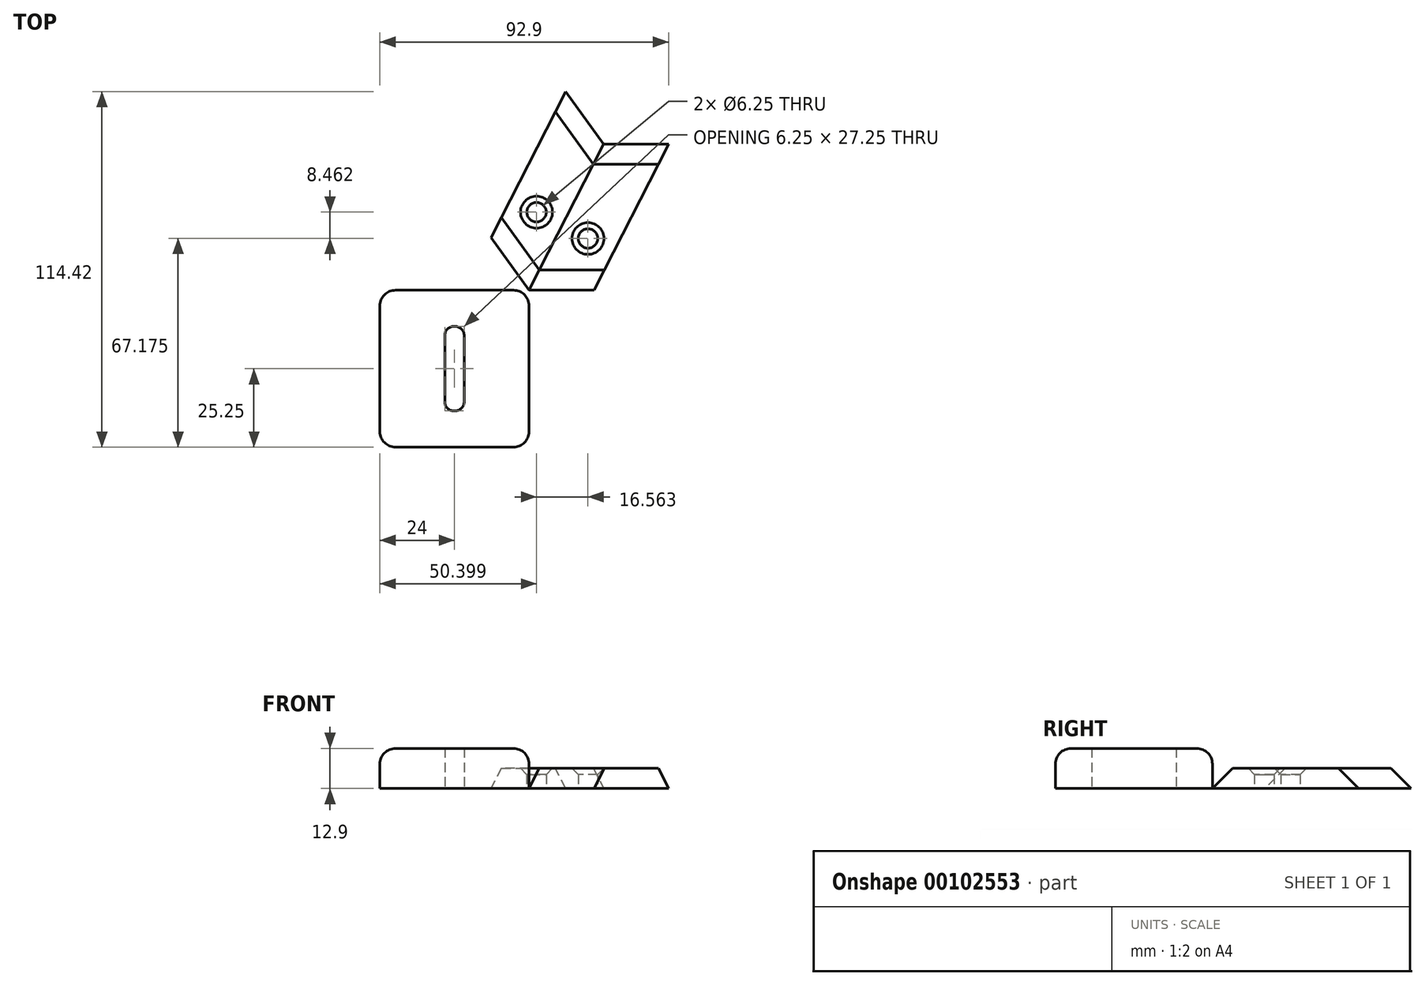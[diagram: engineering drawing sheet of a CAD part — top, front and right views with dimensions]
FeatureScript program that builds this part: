
annotation { "Feature Type Name" : "Feature", "Feature Type Description" : "" }
export const myFeature = defineFeature(function(context is Context, id is Id, definition is map)
    precondition{}
    {
        {
            var Q0;
            Q0=qCreatedBy(makeId("Top.planeOp"),FACE);
            var sketch = newSketch(context, id + "F0", { "sketchPlane" : qUnion([Q0])});
            skLineSegment(sketch, "E0.bottom", {"start": v(-43, -50.5) * mm, "end": v(-5, -50.5) * mm});
            skLineSegment(sketch, "E0.top", {"start": v(-43, 0) * mm, "end": v(-5, 0) * mm});
            skLineSegment(sketch, "E0.left", {"start": v(-48, -45.5) * mm, "end": v(-48, -5) * mm});
            skLineSegment(sketch, "E0.right", {"start": v(0, -45.5) * mm, "end": v(0, -5) * mm});
            skLineSegment(sketch, "E1.bottom", {"start": v(-24.13, -11.62) * mm, "end": v(-23.87, -11.62) * mm});
            skLineSegment(sketch, "E1.top", {"start": v(-24.13, -38.88) * mm, "end": v(-23.87, -38.88) * mm});
            skLineSegment(sketch, "E1.left", {"start": v(-27.13, -14.62) * mm, "end": v(-27.13, -35.88) * mm});
            skLineSegment(sketch, "E1.right", {"start": v(-20.87, -14.62) * mm, "end": v(-20.87, -35.88) * mm});
            skPoint(sketch, "E2", {"position": v(-24, -11.62) * mm});
            skPoint(sketch, "E3", {"position": v(-20.87, -25.25) * mm});
            skPoint(sketch, "E4", {"position": v(-27.13, -25.25) * mm});
            skPoint(sketch, "E5", {"position": v(-24, -38.88) * mm});
            skPoint(sketch, "E6", {"position": v(-24, 0) * mm});
            skPoint(sketch, "E7", {"position": v(-24, -50.5) * mm});
            skPoint(sketch, "E8", {"position": v(0, -25.25) * mm});
            skPoint(sketch, "E9", {"position": v(-48, -25.25) * mm});
            skPoint(sketch, "E10.visualSharp", {"position": v(-27.13, -11.62) * mm});
            skArc(sketch, "E10.filletArc", {"start": v(-24.13, -11.62) * mm, "mid": v(-26.25, -12.5) * mm, "end": v(-27.13, -14.62) * mm});
            skPoint(sketch, "E11.visualSharp", {"position": v(-20.87, -11.62) * mm});
            skArc(sketch, "E11.filletArc", {"start": v(-20.87, -14.62) * mm, "mid": v(-21.75, -12.5) * mm, "end": v(-23.87, -11.62) * mm});
            skPoint(sketch, "E12.visualSharp", {"position": v(-27.13, -38.88) * mm});
            skArc(sketch, "E12.filletArc", {"start": v(-27.13, -35.88) * mm, "mid": v(-26.25, -38) * mm, "end": v(-24.13, -38.88) * mm});
            skPoint(sketch, "E13.visualSharp", {"position": v(-20.87, -38.88) * mm});
            skArc(sketch, "E13.filletArc", {"start": v(-23.87, -38.88) * mm, "mid": v(-21.75, -38) * mm, "end": v(-20.87, -35.88) * mm});
            skPoint(sketch, "E14.visualSharp", {"position": v(-48, 0) * mm});
            skArc(sketch, "E14.filletArc", {"start": v(-43, 0) * mm, "mid": v(-46.54, -1.46) * mm, "end": v(-48, -5) * mm});
            skPoint(sketch, "E15.visualSharp", {"position": v(-48, -50.5) * mm});
            skArc(sketch, "E15.filletArc", {"start": v(-48, -45.5) * mm, "mid": v(-46.54, -49.04) * mm, "end": v(-43, -50.5) * mm});
            skPoint(sketch, "E16.visualSharp", {"position": v(0, -50.5) * mm});
            skArc(sketch, "E16.filletArc", {"start": v(-5, -50.5) * mm, "mid": v(-1.46, -49.04) * mm, "end": v(0, -45.5) * mm});
            skPoint(sketch, "E17.visualSharp", {"position": v(0, 0) * mm});
            skArc(sketch, "E17.filletArc", {"start": v(0, -5) * mm, "mid": v(-1.46, -1.46) * mm, "end": v(-5, 0) * mm});
            skSolve(sketch);
        }
        {
            var Q0;
            Q0=makeQuery(id+"F0.imprint","IMPRINT",FACE,{"disambiguationData":[TD([[makeQuery(id+"F0.imprint","IMPRINT",EDGE,{"derivedFrom":sQuery(id+"F0.wireOp",EDGE,"E0.bottom")}),1.0]])]});
            extrude(context, id + "F1", {"entities" : qUnion([Q0]), "depth" : 12.9 * mm});
        }
        {
            var Q0;
            Q0=makeQuery(id+"F1.opExtrude","CAP_EDGE",EDGE,{"disambiguationData":[OSD([sQuery(id+"F0.wireOp",EDGE,"E0.right")])],"isStart":false});
            var Q1;
            Q1=makeQuery(id+"F1.opExtrude","CAP_EDGE",EDGE,{"disambiguationData":[OSD([sQuery(id+"F0.wireOp",EDGE,"E16.filletArc")])],"isStart":false});
            var Q2;
            Q2=makeQuery(id+"F1.opExtrude","CAP_EDGE",EDGE,{"disambiguationData":[OSD([sQuery(id+"F0.wireOp",EDGE,"E0.bottom")])],"isStart":false});
            var Q3;
            Q3=makeQuery(id+"F1.opExtrude","CAP_EDGE",EDGE,{"disambiguationData":[OSD([sQuery(id+"F0.wireOp",EDGE,"E15.filletArc")])],"isStart":false});
            var Q4;
            Q4=makeQuery(id+"F1.opExtrude","CAP_EDGE",EDGE,{"disambiguationData":[OSD([sQuery(id+"F0.wireOp",EDGE,"E0.left")])],"isStart":false});
            var Q5;
            Q5=makeQuery(id+"F1.opExtrude","CAP_EDGE",EDGE,{"disambiguationData":[OSD([sQuery(id+"F0.wireOp",EDGE,"E14.filletArc")])],"isStart":false});
            var Q6;
            Q6=makeQuery(id+"F1.opExtrude","CAP_EDGE",EDGE,{"disambiguationData":[OSD([sQuery(id+"F0.wireOp",EDGE,"E0.top")])],"isStart":false});
            var Q7;
            Q7=makeQuery(id+"F1.opExtrude","CAP_EDGE",EDGE,{"disambiguationData":[OSD([sQuery(id+"F0.wireOp",EDGE,"E17.filletArc")])],"isStart":false});
            fillet(context, id + "F2", {"entities" : qUnion([Q0, Q1, Q2, Q3, Q4, Q5, Q6, Q7]), "radius" : 5 * mm, "tangentPropagation" : true, "allowEdgeOverflow" : false});
        }
        {
            var Q0;
            Q0=qCreatedBy(makeId("Top.planeOp"),FACE);
            var sketch = newSketch(context, id + "F3", { "sketchPlane" : qUnion([Q0])});
            skLineSegment(sketch, "E18", {"start": v(0, 0) * mm, "end": v(20.89, 0) * mm});
            skLineSegment(sketch, "E19", {"start": v(20.89, 0) * mm, "end": v(44.9, 47) * mm});
            skLineSegment(sketch, "E20", {"start": v(44.9, 47) * mm, "end": v(24.01, 47) * mm});
            skLineSegment(sketch, "E21", {"start": v(24.01, 47) * mm, "end": v(0, 0) * mm});
            skCircle(sketch, "E22", {"center": v(18.96, 16.67) * mm, "radius": 3.12 * mm});
            skLineSegment(sketch, "E23", {"start": v(34.46, 47) * mm, "end": v(10.44, 0) * mm, "construction": true});
            skSolve(sketch);
        }
        {
            var Q0;
            Q0=makeQuery(id+"F3.imprint","IMPRINT",FACE,{"disambiguationData":[TD([[makeQuery(id+"F3.imprint","IMPRINT",EDGE,{"derivedFrom":sQuery(id+"F3.wireOp",EDGE,"E18")}),1.0]])]});
            extrude(context, id + "F4", {"entities" : qUnion([Q0]), "depth" : 6.5 * mm});
        }
        {
            var Q0;
            Q0=makeQuery(id+"F4.opExtrude","CAP_EDGE",EDGE,{"disambiguationData":[OSD([sQuery(id+"F3.wireOp",EDGE,"E18")])],"isStart":false});
            var Q1;
            Q1=makeQuery(id+"F4.opExtrude","CAP_EDGE",EDGE,{"disambiguationData":[OSD([sQuery(id+"F3.wireOp",EDGE,"E20")])],"isStart":false});
            chamfer(context, id + "F5", {"entities" : qUnion([Q0, Q1]), "width" : 6.5 * mm, "tangentPropagation" : true});
        }
        {
            var Q0;
            Q0=makeQuery(id+"F4.opExtrude","CAP_EDGE",EDGE,{"disambiguationData":[OSD([sQuery(id+"F3.wireOp",EDGE,"E22")])],"isStart":false});
            chamfer(context, id + "F6", {"entities" : qUnion([Q0]), "width" : 2 * mm, "tangentPropagation" : true});
        }
        {
            var Q0;
            Q0=makeQuery(id+"F4.opExtrude","SWEPT_BODY",BODY,{"disambiguationData":[OSD([sQuery(id+"F3.wireOp",EDGE,"E18"),sQuery(id+"F3.wireOp",EDGE,"E19"),sQuery(id+"F3.wireOp",EDGE,"E20"),sQuery(id+"F3.wireOp",EDGE,"E21"),sQuery(id+"F3.wireOp",EDGE,"E22")])]});
            var Q1;
            Q1=makeQuery(id+"F4.opExtrude","SWEPT_FACE",FACE,{"disambiguationData":[OSD([sQuery(id+"F3.wireOp",EDGE,"E21")])]});
            mirror(context, id + "F7", {"entities" : qUnion([Q0]), "mirrorPlane" : qUnion([Q1])});
        }
    });
